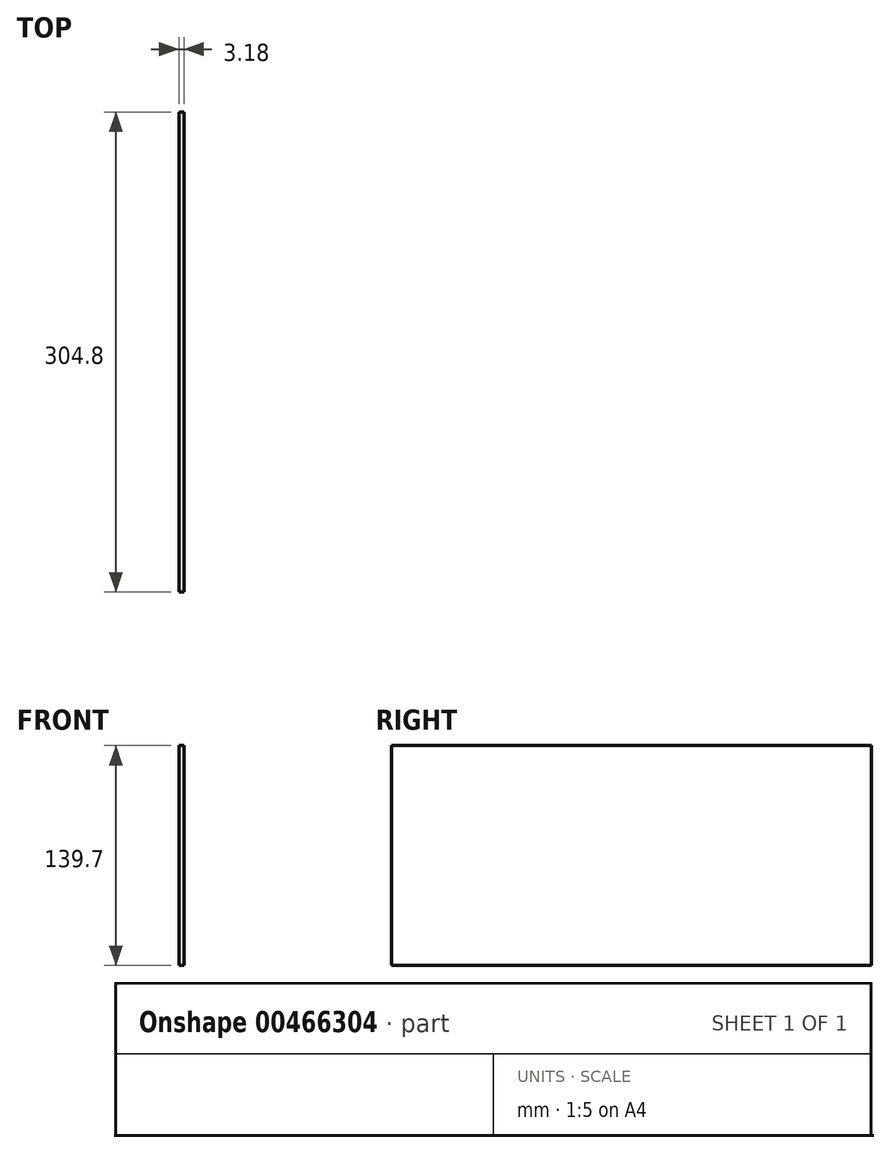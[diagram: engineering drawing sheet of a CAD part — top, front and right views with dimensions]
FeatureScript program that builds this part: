
annotation { "Feature Type Name" : "Feature", "Feature Type Description" : "" }
export const myFeature = defineFeature(function(context is Context, id is Id, definition is map)
    precondition{}
    {
        {
            var Q0;
            Q0=qCreatedBy(makeId("Front.planeOp"),FACE);
            var sketch = newSketch(context, id + "F0", { "sketchPlane" : qUnion([Q0])});
            skLineSegment(sketch, "E0", {"start": v(-45.8, 77.77) * mm, "end": v(-45.8, -61.93) * mm});
            skLineSegment(sketch, "E1", {"start": v(-45.8, -61.93) * mm, "end": v(-48.97, -61.93) * mm});
            skLineSegment(sketch, "E2", {"start": v(-48.97, 77.77) * mm, "end": v(-48.97, -61.93) * mm});
            skLineSegment(sketch, "E3", {"start": v(-45.8, 77.77) * mm, "end": v(-48.97, 77.77) * mm});
            skSolve(sketch);
        }
        {
            var Q0;
            Q0=makeQuery(id+"F0.imprint","IMPRINT",FACE,{"disambiguationData":[TD([[makeQuery(id+"F0.imprint","IMPRINT",EDGE,{"derivedFrom":sQuery(id+"F0.wireOp",EDGE,"E0")}),-1.0]])]});
            extrude(context, id + "F1", {"entities" : qUnion([Q0]), "depth" : 304.8 * mm, "offsetDistance" : 25.4 * mm});
        }
    });
